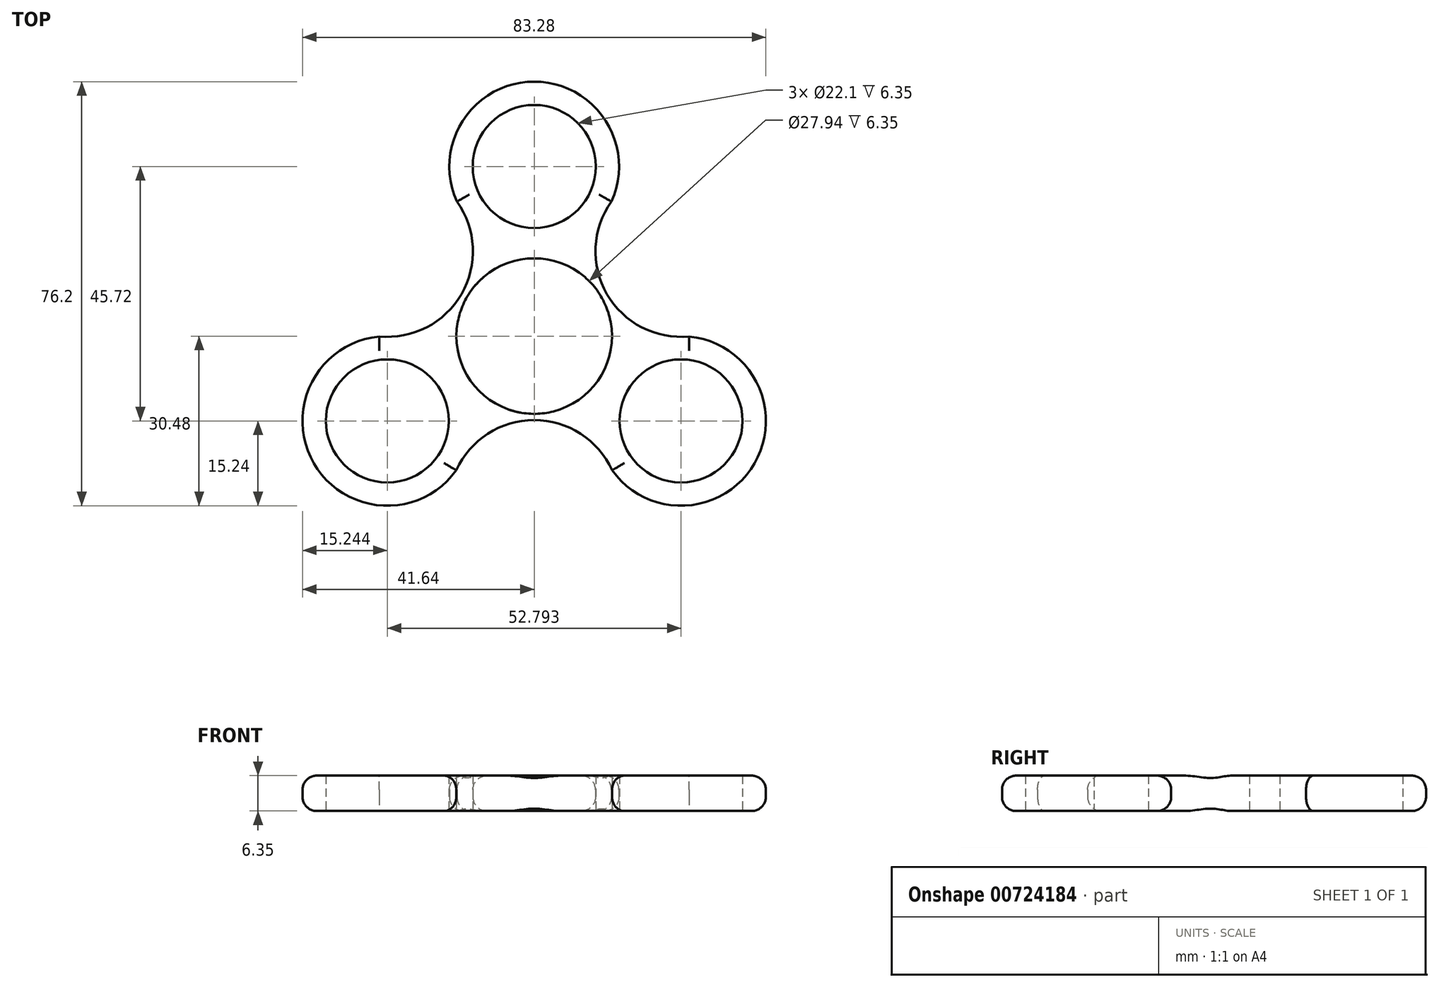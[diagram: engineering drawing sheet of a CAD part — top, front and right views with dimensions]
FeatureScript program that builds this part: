
annotation { "Feature Type Name" : "Feature", "Feature Type Description" : "" }
export const myFeature = defineFeature(function(context is Context, id is Id, definition is map)
    precondition{}
    {
        {
            var Q0;
            Q0=qCreatedBy(makeId("Top.planeOp"),FACE);
            var sketch = newSketch(context, id + "F0", { "sketchPlane" : qUnion([Q0])});
            skCircle(sketch, "E0", {"center": v(0, 0) * mm, "radius": 13.97 * mm});
            skCircle(sketch, "E1", {"center": v(0, 0) * mm, "radius": 11.05 * mm});
            skLineSegment(sketch, "E2", {"start": v(0, -1.08) * mm, "end": v(0, 0) * mm});
            skLineSegment(sketch, "E3", {"start": v(0, 0) * mm, "end": v(0, 30.48) * mm});
            skCircle(sketch, "E4", {"center": v(0, 30.48) * mm, "radius": 11.05 * mm});
            skCircle(sketch, "E5", {"center": v(0, 30.48) * mm, "radius": 15.24 * mm});
            skCircle(sketch, "E6.1.0", {"center": v(-26.4, -15.24) * mm, "radius": 15.24 * mm});
            skCircle(sketch, "E6.1.1", {"center": v(-26.4, -15.24) * mm, "radius": 11.05 * mm});
            skCircle(sketch, "E6.2.0", {"center": v(26.4, -15.24) * mm, "radius": 15.24 * mm});
            skCircle(sketch, "E6.2.1", {"center": v(26.4, -15.24) * mm, "radius": 11.05 * mm});
            skArc(sketch, "E7", {"start": v(-27.87, -0.07) * mm, "mid": v(-13.08, 7.55) * mm, "end": v(-13.87, 24.17) * mm});
            skArc(sketch, "E8.1.0", {"start": v(14, -24.1) * mm, "mid": v(0, -15.1) * mm, "end": v(-14, -24.1) * mm});
            skArc(sketch, "E8.2.0", {"start": v(13.87, 24.17) * mm, "mid": v(13.08, 7.55) * mm, "end": v(27.87, -0.07) * mm});
            skSolve(sketch);
        }
        {
            var Q0;
            Q0=makeQuery(id+"F0.imprint","IMPRINT",FACE,{"disambiguationData":[TD([[makeQuery(id+"F0.imprint","IMPRINT",EDGE,{"derivedFrom":sQuery(id+"F0.wireOp",EDGE,"E4")}),-1.0]])]});
            var Q1;
            Q1=makeQuery(id+"F0.imprint","IMPRINT",FACE,{"disambiguationData":[TD([[makeQuery(id+"F0.imprint","IMPRINT",EDGE,{"derivedFrom":sQuery(id+"F0.wireOp",EDGE,"E0")}),-1.0]])]});
            var Q2;
            Q2=makeQuery(id+"F0.imprint","IMPRINT",FACE,{"disambiguationData":[TD([[makeQuery(id+"F0.imprint","IMPRINT",EDGE,{"derivedFrom":sQuery(id+"F0.wireOp",EDGE,"E6.1.1")}),-1.0]])]});
            var Q3;
            Q3=makeQuery(id+"F0.imprint","IMPRINT",FACE,{"disambiguationData":[TD([[makeQuery(id+"F0.imprint","IMPRINT",EDGE,{"derivedFrom":sQuery(id+"F0.wireOp",EDGE,"E6.2.1")}),-1.0]])]});
            extrude(context, id + "F1", {"entities" : qUnion([Q0, Q1, Q2, Q3]), "depth" : 6.35 * mm, "offsetDistance" : 25.4 * mm});
        }
        {
            var Q0;
            Q0=makeQuery(id+"F1.opExtrude","CAP_EDGE",EDGE,{"disambiguationData":[OSD([sQuery(id+"F0.wireOp",EDGE,"E5")])],"isStart":false});
            var Q1;
            Q1=makeQuery(id+"F1.opExtrude","CAP_EDGE",EDGE,{"disambiguationData":[OSD([sQuery(id+"F0.wireOp",EDGE,"E7")])],"isStart":false});
            var Q2;
            Q2=makeQuery(id+"F1.opExtrude","CAP_EDGE",EDGE,{"disambiguationData":[OSD([sQuery(id+"F0.wireOp",EDGE,"E6.1.0")])],"isStart":false});
            var Q3;
            Q3=makeQuery(id+"F1.opExtrude","CAP_EDGE",EDGE,{"disambiguationData":[OSD([sQuery(id+"F0.wireOp",EDGE,"E8.1.0")])],"isStart":false});
            var Q4;
            Q4=makeQuery(id+"F1.opExtrude","CAP_EDGE",EDGE,{"disambiguationData":[OSD([sQuery(id+"F0.wireOp",EDGE,"E6.2.0")])],"isStart":false});
            var Q5;
            Q5=makeQuery(id+"F1.opExtrude","CAP_EDGE",EDGE,{"disambiguationData":[OSD([sQuery(id+"F0.wireOp",EDGE,"E8.2.0")])],"isStart":false});
            fillet(context, id + "F2", {"entities" : qUnion([Q0, Q1, Q2, Q3, Q4, Q5]), "radius" : 2.54 * mm, "tangentPropagation" : true, "allowEdgeOverflow" : false});
        }
        {
            var Q0;
            Q0=makeQuery(id+"F1.opExtrude","CAP_EDGE",EDGE,{"disambiguationData":[OSD([sQuery(id+"F0.wireOp",EDGE,"E6.2.0")])],"isStart":true});
            var Q1;
            Q1=makeQuery(id+"F1.opExtrude","CAP_EDGE",EDGE,{"disambiguationData":[OSD([sQuery(id+"F0.wireOp",EDGE,"E8.2.0")])],"isStart":true});
            var Q2;
            Q2=makeQuery(id+"F1.opExtrude","CAP_EDGE",EDGE,{"disambiguationData":[OSD([sQuery(id+"F0.wireOp",EDGE,"E5")])],"isStart":true});
            var Q3;
            Q3=makeQuery(id+"F1.opExtrude","CAP_EDGE",EDGE,{"disambiguationData":[OSD([sQuery(id+"F0.wireOp",EDGE,"E6.1.0")])],"isStart":true});
            var Q4;
            Q4=makeQuery(id+"F1.opExtrude","CAP_EDGE",EDGE,{"disambiguationData":[OSD([sQuery(id+"F0.wireOp",EDGE,"E7")])],"isStart":true});
            var Q5;
            Q5=makeQuery(id+"F1.opExtrude","CAP_EDGE",EDGE,{"disambiguationData":[OSD([sQuery(id+"F0.wireOp",EDGE,"E8.1.0")])],"isStart":true});
            fillet(context, id + "F3", {"entities" : qUnion([Q0, Q1, Q2, Q3, Q4, Q5]), "radius" : 2.54 * mm, "tangentPropagation" : true, "allowEdgeOverflow" : false});
        }
    });
